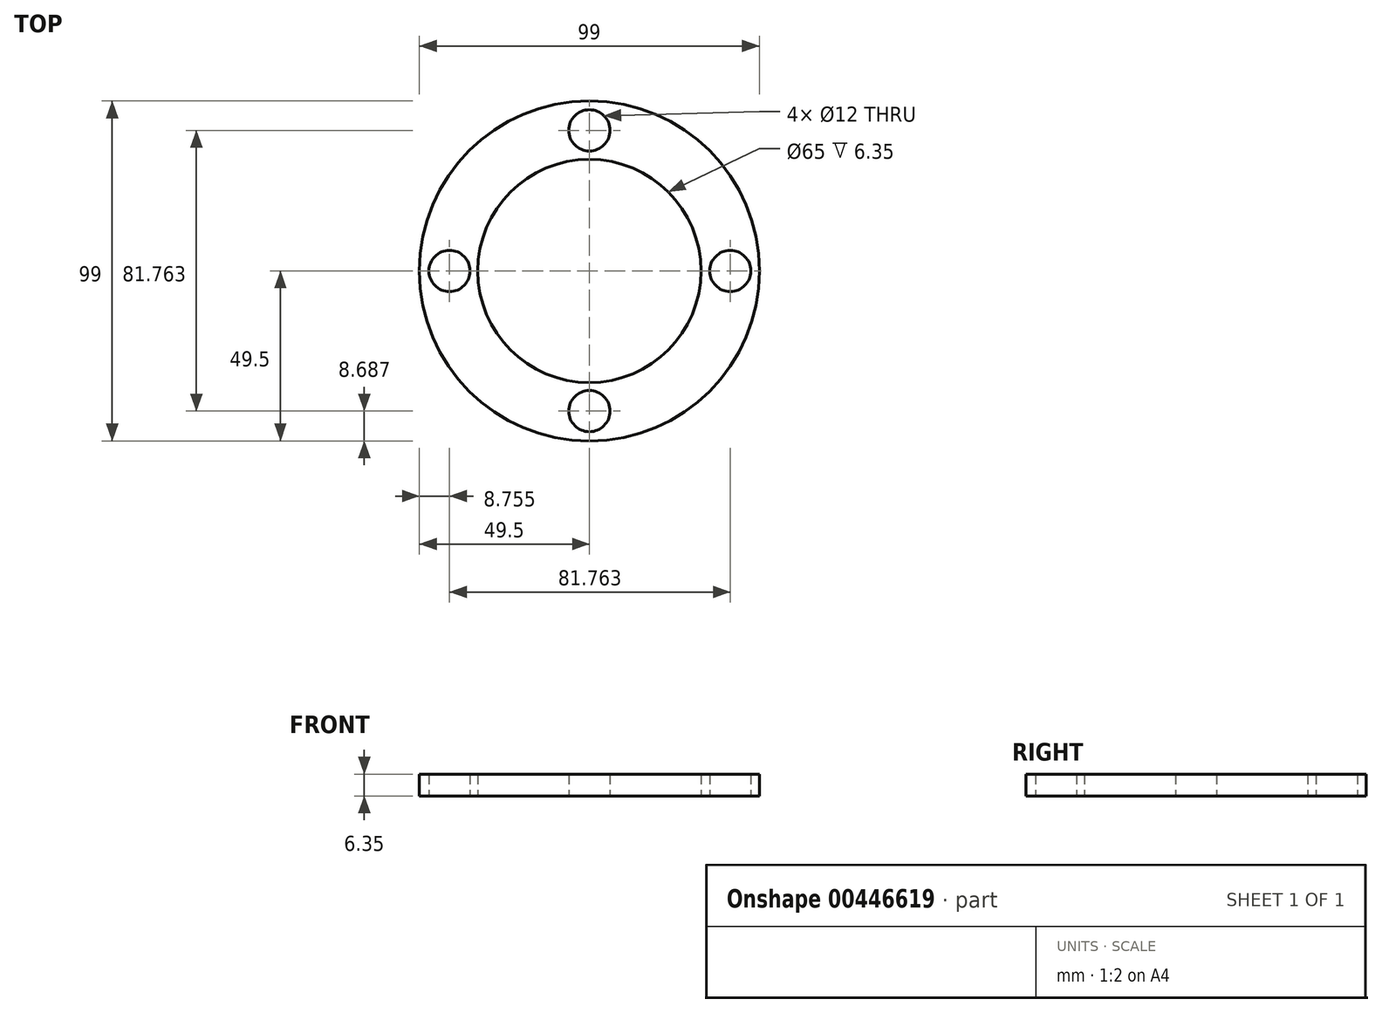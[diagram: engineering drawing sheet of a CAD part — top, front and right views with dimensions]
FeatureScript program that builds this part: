
annotation { "Feature Type Name" : "Feature", "Feature Type Description" : "" }
export const myFeature = defineFeature(function(context is Context, id is Id, definition is map)
    precondition{}
    {
        {
            var Q0;
            Q0=qCreatedBy(makeId("Top.planeOp"),FACE);
            var sketch = newSketch(context, id + "F0", { "sketchPlane" : qUnion([Q0])});
            skCircle(sketch, "E0", {"center": v(0, 0) * mm, "radius": 49.5 * mm});
            skCircle(sketch, "E1", {"center": v(0, 0) * mm, "radius": 32.5 * mm});
            skCircle(sketch, "E2", {"center": v(-40.74, 0) * mm, "radius": 6 * mm});
            skCircle(sketch, "E3", {"center": v(41.02, 0) * mm, "radius": 6 * mm});
            skCircle(sketch, "E4", {"center": v(0, 40.95) * mm, "radius": 6 * mm});
            skCircle(sketch, "E5", {"center": v(0, -40.81) * mm, "radius": 6 * mm});
            skSolve(sketch);
        }
        {
            var Q0;
            Q0 = qSketchRegion(id + "F0", true);
            extrude(context, id + "F1", {"entities" : qUnion([Q0]), "depth" : 6.35 * mm});
        }
    });
